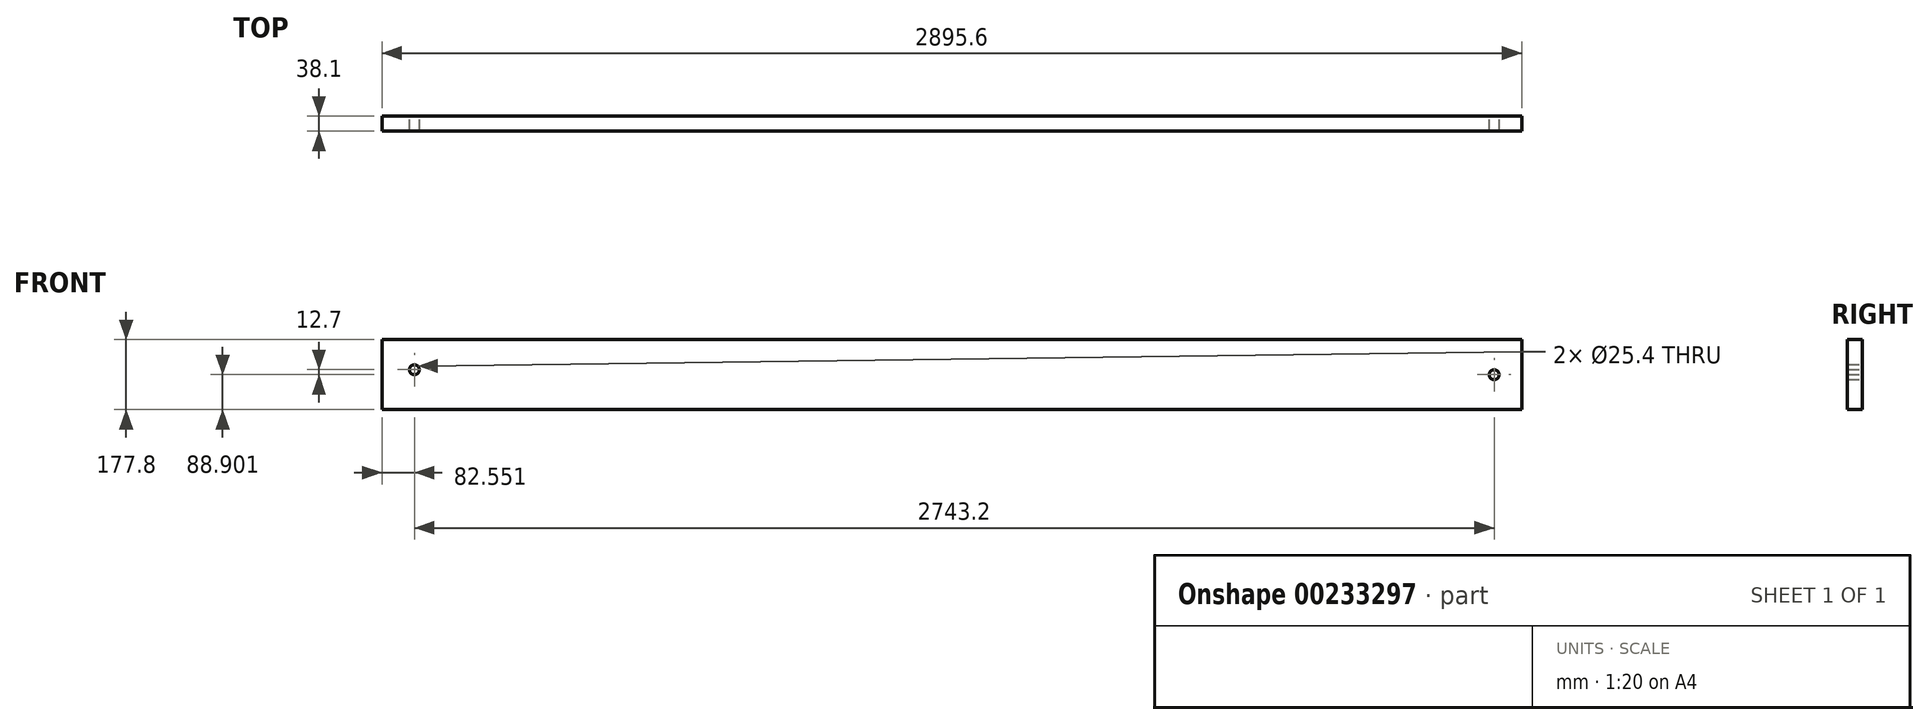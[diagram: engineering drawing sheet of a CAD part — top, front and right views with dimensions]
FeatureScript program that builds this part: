
annotation { "Feature Type Name" : "Feature", "Feature Type Description" : "" }
export const myFeature = defineFeature(function(context is Context, id is Id, definition is map)
    precondition{}
    {
        {
            var Q0;
            Q0=qCreatedBy(makeId("Front.planeOp"),FACE);
            var sketch = newSketch(context, id + "F0", { "sketchPlane" : qUnion([Q0])});
            skLineSegment(sketch, "E0.bottom", {"start": v(-1385.62, -225.92) * mm, "end": v(1509.98, -225.92) * mm});
            skLineSegment(sketch, "E0.top", {"start": v(-1385.62, -403.72) * mm, "end": v(1509.98, -403.72) * mm});
            skLineSegment(sketch, "E0.left", {"start": v(-1385.62, -225.92) * mm, "end": v(-1385.62, -403.72) * mm});
            skLineSegment(sketch, "E0.right", {"start": v(1509.98, -225.92) * mm, "end": v(1509.98, -403.72) * mm});
            skCircle(sketch, "E1", {"center": v(-1303.07, -302.12) * mm, "radius": 12.7 * mm});
            skCircle(sketch, "E2", {"center": v(1440.13, -314.82) * mm, "radius": 12.7 * mm});
            skSolve(sketch);
        }
        {
            var Q0;
            Q0=makeQuery(id+"F0.imprint","IMPRINT",FACE,{"disambiguationData":[TD([[makeQuery(id+"F0.imprint","IMPRINT",EDGE,{"derivedFrom":sQuery(id+"F0.wireOp",EDGE,"E0.bottom")}),-1.0]])]});
            extrude(context, id + "F1", {"entities" : qUnion([Q0]), "depth" : 38.1 * mm});
        }
    });
